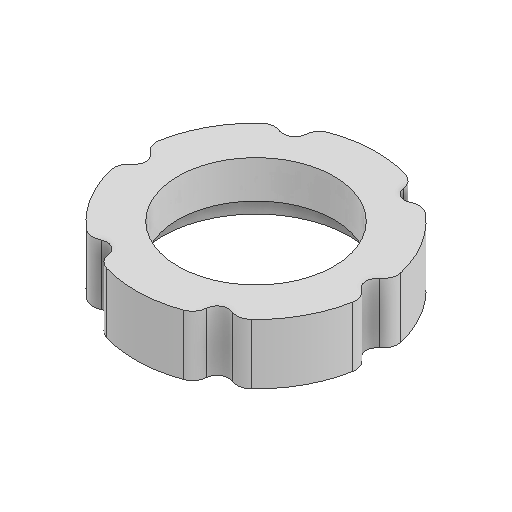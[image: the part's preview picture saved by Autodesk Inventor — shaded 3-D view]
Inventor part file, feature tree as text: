
AUTODESK INVENTOR PART (.ipt)
format: ipt  version: 2025 (Build 290162000, 162)  size: 154,112 bytes
history: native  units: mm
features: sketch x3, extrude x2, fillet x1
ambient origin geometry x8: Origin, YZ Plane, XZ Plane, XY Plane, X Axis, Y Axis, Z Axis, Center Point
bodies: Solid1 (feature_tree)
feature tree (6):
  extrude  "Extrusion1"  Depth=10.0mm TaperAngle=0.0deg
  fillet  "Fillet1"  Radius=3.0mm
  extrude  "Extrusion2"  Depth=2.0mm
  sketch  "Sketch1"  dims[d0=20.75mm d1=10.0mm d2=8.0mm d3=0.0mm d4=3.0mm]
  sketch  "Sketch Circular Pattern1"  dims[d5=60.0mm d7=360.0deg d9=2.0mm]
  sketch  "Sketch2"  dims[d10=16.0mm d11=25.0mm d12=3.0mm d13=0.0mm]
